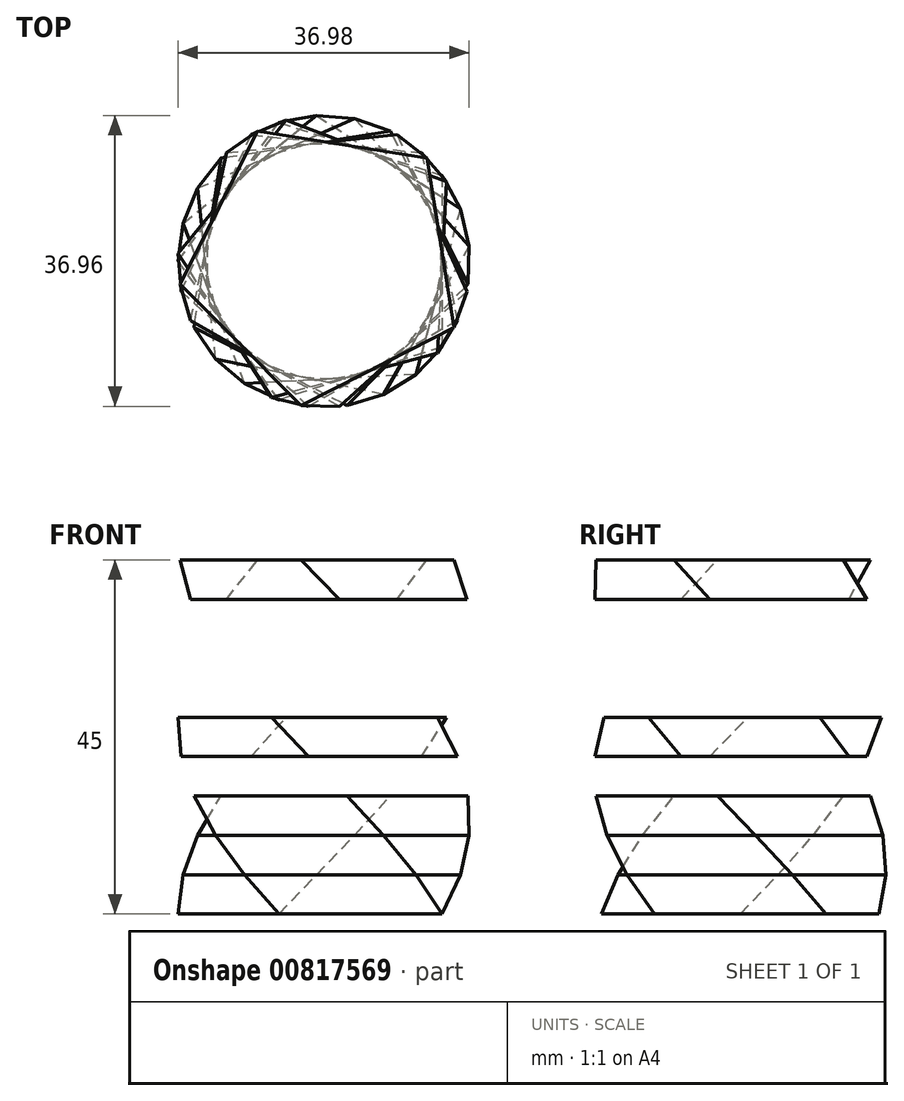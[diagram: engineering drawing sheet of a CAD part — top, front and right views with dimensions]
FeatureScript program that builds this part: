
annotation { "Feature Type Name" : "Feature", "Feature Type Description" : "" }
export const myFeature = defineFeature(function(context is Context, id is Id, definition is map)
    precondition{}
    {
        {
            var Q0;
            Q0=qCreatedBy(makeId("Top.planeOp"),FACE);
            var sketch = newSketch(context, id + "F0", { "sketchPlane" : qUnion([Q0])});
            skCircle(sketch, "E0.cCircle", {"center": v(0, 0) * mm, "radius": 15 * mm, "construction": true});
            skLineSegment(sketch, "E0.0", {"start": v(15, 10.9) * mm, "end": v(15, -10.9) * mm});
            skLineSegment(sketch, "E0.1", {"start": v(15, -10.9) * mm, "end": v(-5.73, -17.63) * mm});
            skLineSegment(sketch, "E0.2", {"start": v(-5.73, -17.63) * mm, "end": v(-18.54, 0) * mm});
            skLineSegment(sketch, "E0.3", {"start": v(-18.54, 0) * mm, "end": v(-5.73, 17.63) * mm});
            skLineSegment(sketch, "E0.4", {"start": v(-5.73, 17.63) * mm, "end": v(15, 10.9) * mm});
            skPoint(sketch, "E0.0.midPoint", {"position": v(15, 0) * mm});
            skSolve(sketch);
        }
        {
            var Q0;
            Q0=qCreatedBy(makeId("Top.planeOp"),FACE);
            cPlane(context, id + "F1", {"entities" : qUnion([Q0]), "cplaneType" : CPlaneType.OFFSET, "offset" : 5 * mm, "width" : 150 * mm, "height" : 150 * mm});
        }
        {
            var Q0;
            Q0=qCreatedBy(id+"F1.planeOp",FACE);
            var sketch = newSketch(context, id + "F2", { "sketchPlane" : qUnion([Q0])});
            skLineSegment(sketch, "E1.0", {"start": v(-17.9, 4.8) * mm, "end": v(-0.97, 18.52) * mm});
            skLineSegment(sketch, "E2.0", {"start": v(-10.1, -15.55) * mm, "end": v(-17.9, 4.8) * mm});
            skLineSegment(sketch, "E3.0", {"start": v(11.67, -14.4) * mm, "end": v(-10.1, -15.55) * mm});
            skLineSegment(sketch, "E4.0", {"start": v(17.3, 6.64) * mm, "end": v(11.67, -14.4) * mm});
            skLineSegment(sketch, "E5.0", {"start": v(-0.97, 18.52) * mm, "end": v(17.3, 6.64) * mm});
            skPoint(sketch, "E6.0", {"position": v(0, 0) * mm});
            skSolve(sketch);
        }
        {
            var Q0;
            Q0=qCreatedBy(makeId("Front.planeOp"),FACE);
            var sketch = newSketch(context, id + "F3", { "sketchPlane" : qUnion([Q0])});
            skLineSegment(sketch, "E7", {"start": v(0, 0) * mm, "end": v(0, 71.4) * mm, "construction": true});
            skSolve(sketch);
        }
        {
            var Q0;
            Q0=makeQuery(id+"F0.imprint","IMPRINT",FACE,{"disambiguationData":[TD([[makeQuery(id+"F0.imprint","IMPRINT",EDGE,{"derivedFrom":sQuery(id+"F0.wireOp",EDGE,"E0.0")}),-1.0]])]});
            var Q1;
            Q1=makeQuery(id+"F2.imprint","IMPRINT",FACE,{"disambiguationData":[TD([[makeQuery(id+"F2.imprint","IMPRINT",EDGE,{"derivedFrom":sQuery(id+"F2.wireOp",EDGE,"E1.0")}),-1.0]])]});
            loft(context, id + "F4", {"sheetProfilesArray" : [{ "sheetProfileEntities" : qUnion([Q0]) }, { "sheetProfileEntities" : qUnion([Q1]) }]});
        }
        {
            var Q0;
            Q0=makeQuery(id+"F4.opLoft","SWEPT_BODY",BODY,{"disambiguationData":[OSD([makeQuery(id+"F0.imprint","IMPRINT",FACE,{"disambiguationData":[TD([[makeQuery(id+"F0.imprint","IMPRINT",EDGE,{"derivedFrom":sQuery(id+"F0.wireOp",EDGE,"E0.0")}),-1.0]])]}),makeQuery(id+"F2.imprint","IMPRINT",FACE,{"disambiguationData":[TD([[makeQuery(id+"F2.imprint","IMPRINT",EDGE,{"derivedFrom":sQuery(id+"F2.wireOp",EDGE,"E1.0")}),-1.0]])]})])]});
            var Q1;
            Q1=sQuery(id+"F3.wireOp",EDGE,"E7");
            var Q2;
            Q2=sQuery(id+"F3.wireOp",EDGE,"E7");
            transform(context, id + "F5", {"entities" : qUnion([Q0]), "transformType" : TransformType.TRANSLATION_DISTANCE, "transformDirection" : qUnion([Q2]), "distance" : 5 * mm, "makeCopy" : true});
        }
        {
            var Q0;
            Q0=makeQuery(id+"F5.opPattern","COPY",BODY,{"derivedFrom":makeQuery(id+"F4.opLoft","SWEPT_BODY",BODY,{"disambiguationData":[OSD([makeQuery(id+"F0.imprint","IMPRINT",FACE,{"disambiguationData":[TD([[makeQuery(id+"F0.imprint","IMPRINT",EDGE,{"derivedFrom":sQuery(id+"F0.wireOp",EDGE,"E0.0")}),-1.0]])]}),makeQuery(id+"F2.imprint","IMPRINT",FACE,{"disambiguationData":[TD([[makeQuery(id+"F2.imprint","IMPRINT",EDGE,{"derivedFrom":sQuery(id+"F2.wireOp",EDGE,"E1.0")}),-1.0]])]})])]}),"instanceName":"1"});
            var Q1;
            Q1=sQuery(id+"F3.wireOp",EDGE,"E7");
            transform(context, id + "F6", {"entities" : qUnion([Q0]), "transformType" : TransformType.ROTATION, "transformAxis" : qUnion([Q1]), "angle" : 15 * degree, "oppositeDirection" : true, "makeCopy" : false});
        }
        {
            var Q0;
            Q0=makeQuery(id+"F4.opLoft","SWEPT_BODY",BODY,{"disambiguationData":[OSD([makeQuery(id+"F0.imprint","IMPRINT",FACE,{"disambiguationData":[TD([[makeQuery(id+"F0.imprint","IMPRINT",EDGE,{"derivedFrom":sQuery(id+"F0.wireOp",EDGE,"E0.0")}),-1.0]])]}),makeQuery(id+"F2.imprint","IMPRINT",FACE,{"disambiguationData":[TD([[makeQuery(id+"F2.imprint","IMPRINT",EDGE,{"derivedFrom":sQuery(id+"F2.wireOp",EDGE,"E1.0")}),-1.0]])]})])]});
            transform(context, id + "F7", {"entities" : qUnion([Q0]), "transformType" : TransformType.TRANSLATION_3D, "dx" : 0 * mm, "dy" : 0 * mm, "dz" : 10 * mm, "makeCopy" : true});
        }
        {
            var Q0;
            Q0=makeQuery(id+"F7.opPattern","COPY",BODY,{"derivedFrom":makeQuery(id+"F4.opLoft","SWEPT_BODY",BODY,{"disambiguationData":[OSD([makeQuery(id+"F0.imprint","IMPRINT",FACE,{"disambiguationData":[TD([[makeQuery(id+"F0.imprint","IMPRINT",EDGE,{"derivedFrom":sQuery(id+"F0.wireOp",EDGE,"E0.0")}),-1.0]])]}),makeQuery(id+"F2.imprint","IMPRINT",FACE,{"disambiguationData":[TD([[makeQuery(id+"F2.imprint","IMPRINT",EDGE,{"derivedFrom":sQuery(id+"F2.wireOp",EDGE,"E1.0")}),-1.0]])]})])]}),"instanceName":"1"});
            var Q1;
            Q1=sQuery(id+"F3.wireOp",EDGE,"E7");
            transform(context, id + "F8", {"entities" : qUnion([Q0]), "transformType" : TransformType.ROTATION, "transformAxis" : qUnion([Q1]), "angle" : 30 * degree, "oppositeDirection" : true, "makeCopy" : false});
        }
        {
            var Q0;
            Q0=makeQuery(id+"F4.opLoft","SWEPT_BODY",BODY,{"disambiguationData":[OSD([makeQuery(id+"F0.imprint","IMPRINT",FACE,{"disambiguationData":[TD([[makeQuery(id+"F0.imprint","IMPRINT",EDGE,{"derivedFrom":sQuery(id+"F0.wireOp",EDGE,"E0.0")}),-1.0]])]}),makeQuery(id+"F2.imprint","IMPRINT",FACE,{"disambiguationData":[TD([[makeQuery(id+"F2.imprint","IMPRINT",EDGE,{"derivedFrom":sQuery(id+"F2.wireOp",EDGE,"E1.0")}),-1.0]])]})])]});
            transform(context, id + "F9", {"entities" : qUnion([Q0]), "transformType" : TransformType.TRANSLATION_3D, "dx" : 0 * mm, "dy" : 0 * mm, "dz" : 20 * mm, "makeCopy" : true});
        }
        {
            var Q0;
            Q0=makeQuery(id+"F9.opPattern","COPY",BODY,{"derivedFrom":makeQuery(id+"F4.opLoft","SWEPT_BODY",BODY,{"disambiguationData":[OSD([makeQuery(id+"F0.imprint","IMPRINT",FACE,{"disambiguationData":[TD([[makeQuery(id+"F0.imprint","IMPRINT",EDGE,{"derivedFrom":sQuery(id+"F0.wireOp",EDGE,"E0.0")}),-1.0]])]}),makeQuery(id+"F2.imprint","IMPRINT",FACE,{"disambiguationData":[TD([[makeQuery(id+"F2.imprint","IMPRINT",EDGE,{"derivedFrom":sQuery(id+"F2.wireOp",EDGE,"E1.0")}),-1.0]])]})])]}),"instanceName":"1"});
            var Q1;
            Q1=sQuery(id+"F3.wireOp",EDGE,"E7");
            transform(context, id + "F10", {"entities" : qUnion([Q0]), "transformType" : TransformType.ROTATION, "transformAxis" : qUnion([Q1]), "angle" : 12 * degree, "makeCopy" : false});
        }
        {
            var Q0;
            Q0=makeQuery(id+"F4.opLoft","SWEPT_BODY",BODY,{"disambiguationData":[OSD([makeQuery(id+"F0.imprint","IMPRINT",FACE,{"disambiguationData":[TD([[makeQuery(id+"F0.imprint","IMPRINT",EDGE,{"derivedFrom":sQuery(id+"F0.wireOp",EDGE,"E0.0")}),-1.0]])]}),makeQuery(id+"F2.imprint","IMPRINT",FACE,{"disambiguationData":[TD([[makeQuery(id+"F2.imprint","IMPRINT",EDGE,{"derivedFrom":sQuery(id+"F2.wireOp",EDGE,"E1.0")}),-1.0]])]})])]});
            transform(context, id + "F11", {"entities" : qUnion([Q0]), "transformType" : TransformType.TRANSLATION_3D, "dx" : 0 * mm, "dy" : 0 * mm, "dz" : 40 * mm, "makeCopy" : true});
        }
        {
            var Q0;
            Q0=makeQuery(id+"F11.opPattern","COPY",BODY,{"derivedFrom":makeQuery(id+"F4.opLoft","SWEPT_BODY",BODY,{"disambiguationData":[OSD([makeQuery(id+"F0.imprint","IMPRINT",FACE,{"disambiguationData":[TD([[makeQuery(id+"F0.imprint","IMPRINT",EDGE,{"derivedFrom":sQuery(id+"F0.wireOp",EDGE,"E0.0")}),-1.0]])]}),makeQuery(id+"F2.imprint","IMPRINT",FACE,{"disambiguationData":[TD([[makeQuery(id+"F2.imprint","IMPRINT",EDGE,{"derivedFrom":sQuery(id+"F2.wireOp",EDGE,"E1.0")}),-1.0]])]})])]}),"instanceName":"1"});
            var Q1;
            Q1=sQuery(id+"F3.wireOp",EDGE,"E7");
            transform(context, id + "F12", {"entities" : qUnion([Q0]), "transformType" : TransformType.ROTATION, "transformAxis" : qUnion([Q1]), "angle" : 24 * degree, "makeCopy" : false});
        }
    });
